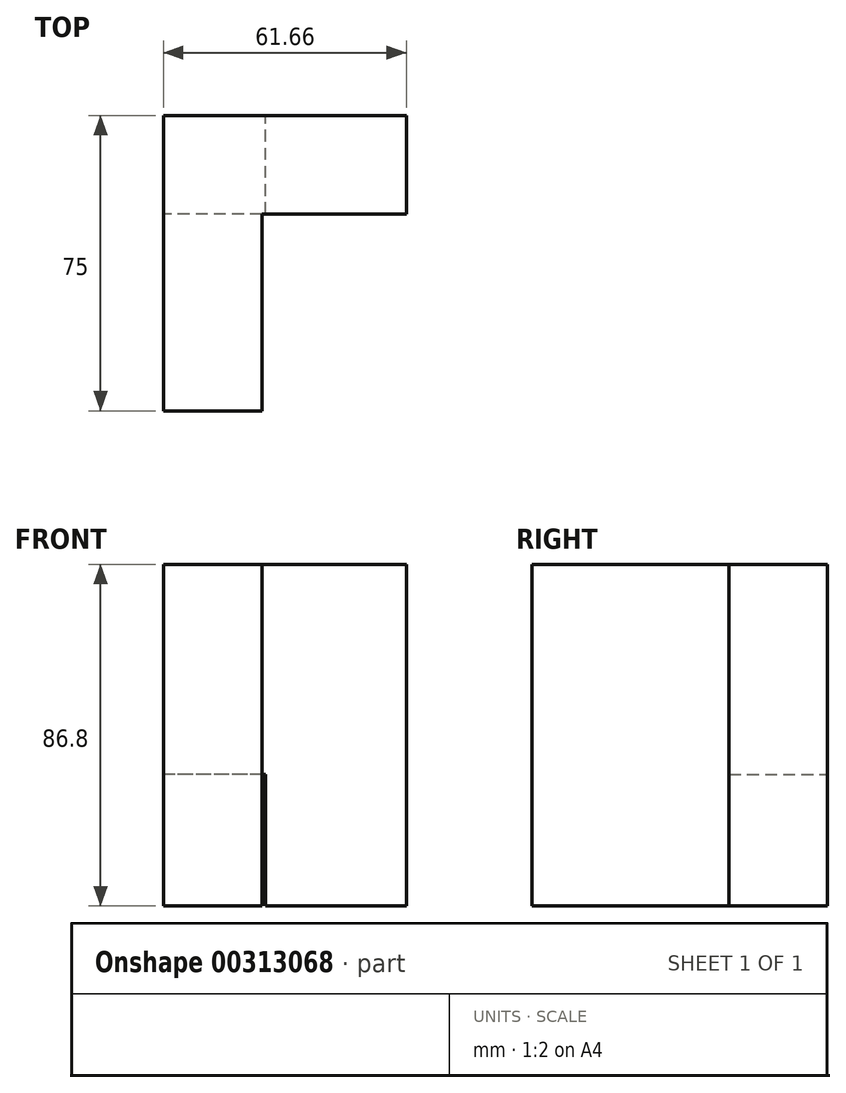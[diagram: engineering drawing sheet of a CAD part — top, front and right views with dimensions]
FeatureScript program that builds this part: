
annotation { "Feature Type Name" : "Feature", "Feature Type Description" : "" }
export const myFeature = defineFeature(function(context is Context, id is Id, definition is map)
    precondition{}
    {
        {
            var Q0;
            Q0=qCreatedBy(makeId("Front.planeOp"),FACE);
            var sketch = newSketch(context, id + "F0", { "sketchPlane" : qUnion([Q0])});
            skLineSegment(sketch, "E0", {"start": v(0, 53.35) * mm, "end": v(61.66, 53.35) * mm});
            skLineSegment(sketch, "E1", {"start": v(61.66, 53.35) * mm, "end": v(61.66, -33.45) * mm});
            skLineSegment(sketch, "E2", {"start": v(61.66, -33.45) * mm, "end": v(25.9, -33.45) * mm});
            skLineSegment(sketch, "E3", {"start": v(25.9, -33.45) * mm, "end": v(25.9, 0) * mm});
            skLineSegment(sketch, "E4", {"start": v(25.9, 0) * mm, "end": v(0, 0) * mm});
            skLineSegment(sketch, "E5", {"start": v(0, 53.35) * mm, "end": v(0, 0) * mm});
            skSolve(sketch);
        }
        {
            var Q0;
            Q0=makeQuery(id+"F0.imprint","IMPRINT",FACE,{"disambiguationData":[TD([[makeQuery(id+"F0.imprint","IMPRINT",EDGE,{"derivedFrom":sQuery(id+"F0.wireOp",EDGE,"E0")}),-1.0]])]});
            extrude(context, id + "F1", {"entities" : qUnion([Q0]), "depth" : 25 * mm});
        }
        {
            var Q0;
            Q0=qCreatedBy(makeId("Right.planeOp"),FACE);
            var sketch = newSketch(context, id + "F2", { "sketchPlane" : qUnion([Q0])});
            skLineSegment(sketch, "E6", {"start": v(-25, 53.35) * mm, "end": v(-75, 53.35) * mm});
            skLineSegment(sketch, "E7", {"start": v(-75, 53.35) * mm, "end": v(-75, -33.45) * mm});
            skLineSegment(sketch, "E8", {"start": v(-75, -33.45) * mm, "end": v(-25, -33.45) * mm});
            skLineSegment(sketch, "E9", {"start": v(-25, -33.45) * mm, "end": v(-25, 53.35) * mm});
            skSolve(sketch);
        }
        {
            var Q0;
            Q0=makeQuery(id+"F2.imprint","IMPRINT",FACE,{"disambiguationData":[TD([[makeQuery(id+"F2.imprint","IMPRINT",EDGE,{"derivedFrom":sQuery(id+"F2.wireOp",EDGE,"E6")}),1.0]])]});
            extrude(context, id + "F3", {"entities" : qUnion([Q0]), "operationType" : NewBodyOperationType.ADD, "depth" : 25 * mm});
        }
    });
